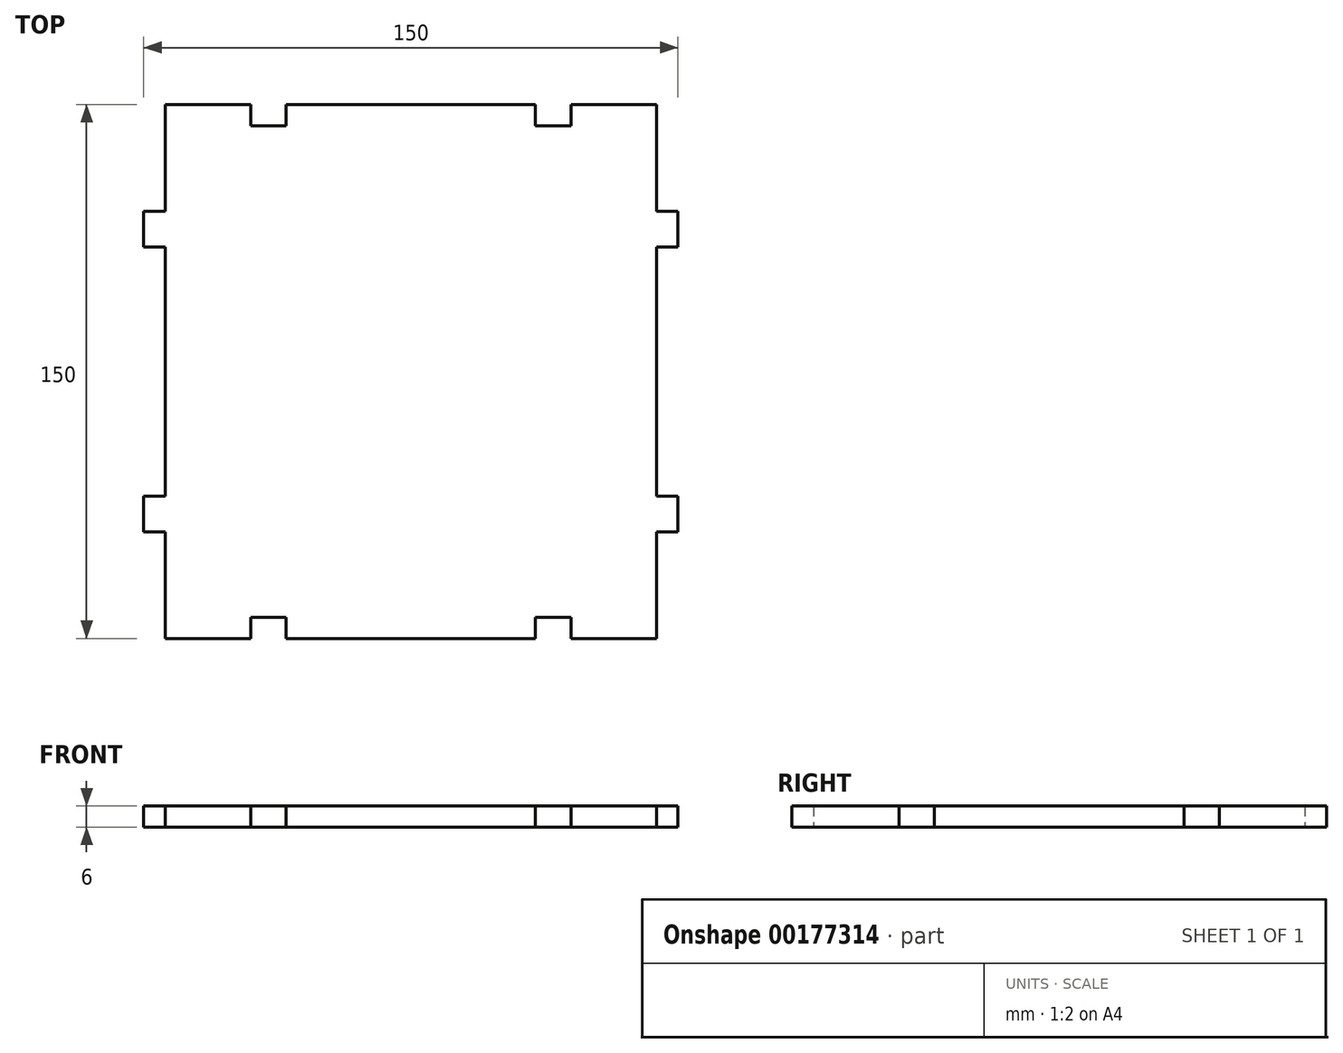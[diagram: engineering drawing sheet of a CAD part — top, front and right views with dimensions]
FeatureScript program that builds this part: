
annotation { "Feature Type Name" : "Feature", "Feature Type Description" : "" }
export const myFeature = defineFeature(function(context is Context, id is Id, definition is map)
    precondition{}
    {
        {
            var Q0;
            Q0=qCreatedBy(makeId("Top.planeOp"),FACE);
            var sketch = newSketch(context, id + "F0", { "sketchPlane" : qUnion([Q0])});
            skPoint(sketch, "E0.middle", {"position": v(4.2, -4.87) * mm});
            skLineSegment(sketch, "E1.bottom", {"start": v(73.2, -79.87) * mm, "end": v(-64.8, -79.87) * mm});
            skLineSegment(sketch, "E1.top", {"start": v(73.2, 70.13) * mm, "end": v(-64.8, 70.13) * mm});
            skLineSegment(sketch, "E1.left", {"start": v(73.2, -79.87) * mm, "end": v(73.2, 70.13) * mm});
            skLineSegment(sketch, "E1.right", {"start": v(-64.8, -79.87) * mm, "end": v(-64.8, 70.13) * mm});
            skLineSegment(sketch, "E2", {"start": v(-64.8, 70.13) * mm, "end": v(-40.8, 70.13) * mm, "construction": true});
            skLineSegment(sketch, "E3", {"start": v(-40.8, 70.13) * mm, "end": v(-40.8, 64.13) * mm});
            skLineSegment(sketch, "E4", {"start": v(-40.8, 64.13) * mm, "end": v(-30.8, 64.13) * mm});
            skLineSegment(sketch, "E5", {"start": v(-30.8, 64.13) * mm, "end": v(-30.8, 70.13) * mm});
            skLineSegment(sketch, "E6", {"start": v(4.2, -4.87) * mm, "end": v(-64.8, -4.87) * mm, "construction": true});
            skLineSegment(sketch, "E7", {"start": v(4.2, -4.87) * mm, "end": v(4.2, 70.13) * mm, "construction": true});
            skLineSegment(sketch, "E8.MirrorCS", {"start": v(49.2, 64.13) * mm, "end": v(39.2, 64.13) * mm});
            skLineSegment(sketch, "E9.MirrorCS", {"start": v(39.2, 64.13) * mm, "end": v(39.2, 70.13) * mm});
            skLineSegment(sketch, "E10.MirrorCS", {"start": v(49.2, 70.13) * mm, "end": v(49.2, 64.13) * mm});
            skLineSegment(sketch, "E11.MirrorCS", {"start": v(4.2, -4.87) * mm, "end": v(73.2, -4.87) * mm, "construction": true});
            skLineSegment(sketch, "E12.MirrorCS", {"start": v(-40.8, 58.13) * mm, "end": v(-40.8, 64.13) * mm});
            skLineSegment(sketch, "E13.MirrorCS", {"start": v(-40.8, -79.87) * mm, "end": v(-40.8, -73.87) * mm});
            skLineSegment(sketch, "E14.MirrorCS", {"start": v(-40.8, -73.87) * mm, "end": v(-30.8, -73.87) * mm});
            skLineSegment(sketch, "E15.MirrorCS", {"start": v(-30.8, -73.87) * mm, "end": v(-30.8, -79.87) * mm});
            skLineSegment(sketch, "E16.MirrorCS", {"start": v(39.2, -73.87) * mm, "end": v(39.2, -79.87) * mm});
            skLineSegment(sketch, "E17.MirrorCS", {"start": v(49.2, -73.87) * mm, "end": v(39.2, -73.87) * mm});
            skLineSegment(sketch, "E18.MirrorCS", {"start": v(49.2, -79.87) * mm, "end": v(49.2, -73.87) * mm});
            skLineSegment(sketch, "E19", {"start": v(-64.8, 70.13) * mm, "end": v(-64.8, 40.13) * mm});
            skLineSegment(sketch, "E20", {"start": v(-64.8, 40.13) * mm, "end": v(-70.8, 40.13) * mm});
            skLineSegment(sketch, "E21", {"start": v(-70.8, 40.13) * mm, "end": v(-70.8, 30.13) * mm});
            skLineSegment(sketch, "E22", {"start": v(-70.8, 30.13) * mm, "end": v(-64.8, 30.13) * mm});
            skLineSegment(sketch, "E23.MirrorCS", {"start": v(-70.8, -39.87) * mm, "end": v(-64.8, -39.87) * mm});
            skLineSegment(sketch, "E24.MirrorCS", {"start": v(-70.8, -49.87) * mm, "end": v(-70.8, -39.87) * mm});
            skLineSegment(sketch, "E25.MirrorCS", {"start": v(-64.8, -49.87) * mm, "end": v(-70.8, -49.87) * mm});
            skLineSegment(sketch, "E26.MirrorCS", {"start": v(73.2, 40.13) * mm, "end": v(79.2, 40.13) * mm});
            skLineSegment(sketch, "E27.MirrorCS", {"start": v(79.2, 40.13) * mm, "end": v(79.2, 30.13) * mm});
            skLineSegment(sketch, "E28.MirrorCS", {"start": v(79.2, 30.13) * mm, "end": v(73.2, 30.13) * mm});
            skLineSegment(sketch, "E29.MirrorCS", {"start": v(79.2, -39.87) * mm, "end": v(73.2, -39.87) * mm});
            skLineSegment(sketch, "E30.MirrorCS", {"start": v(79.2, -49.87) * mm, "end": v(79.2, -39.87) * mm});
            skLineSegment(sketch, "E31.MirrorCS", {"start": v(73.2, -49.87) * mm, "end": v(79.2, -49.87) * mm});
            skLineSegment(sketch, "E32", {"start": v(-64.8, -79.87) * mm, "end": v(-70.8, -79.87) * mm});
            skLineSegment(sketch, "E33", {"start": v(-70.8, -79.87) * mm, "end": v(-70.8, -73.87) * mm});
            skLineSegment(sketch, "E34", {"start": v(-70.8, -73.87) * mm, "end": v(-64.8, -73.87) * mm});
            skLineSegment(sketch, "E35.MirrorCS", {"start": v(-70.8, 70.13) * mm, "end": v(-70.8, 64.13) * mm});
            skLineSegment(sketch, "E36.MirrorCS", {"start": v(-64.8, 70.13) * mm, "end": v(-70.8, 70.13) * mm});
            skLineSegment(sketch, "E37.MirrorCS", {"start": v(-70.8, 64.13) * mm, "end": v(-64.8, 64.13) * mm});
            skLineSegment(sketch, "E38.MirrorCS", {"start": v(73.2, -79.87) * mm, "end": v(79.2, -79.87) * mm});
            skLineSegment(sketch, "E39.MirrorCS", {"start": v(79.2, -79.87) * mm, "end": v(79.2, -73.87) * mm});
            skLineSegment(sketch, "E40.MirrorCS", {"start": v(79.2, -73.87) * mm, "end": v(73.2, -73.87) * mm});
            skLineSegment(sketch, "E41.MirrorCS", {"start": v(73.2, 70.13) * mm, "end": v(79.2, 70.13) * mm});
            skLineSegment(sketch, "E42.MirrorCS", {"start": v(79.2, 70.13) * mm, "end": v(79.2, 64.13) * mm});
            skLineSegment(sketch, "E43.MirrorCS", {"start": v(79.2, 64.13) * mm, "end": v(73.2, 64.13) * mm});
            skSolve(sketch);
        }
        {
            var Q0;
            {var subQ6=sQuery(id+"F0.wireOp",EDGE,"E3");Q0=makeQuery(id+"F0.imprint","IMPRINT",FACE,{"disambiguationData":[TD([[makeQuery(id+"F0.imprint","IMPRINT",EDGE,{"derivedFrom":subQ6}),-1.0]])]});}
            var Q1;
            {var subQ0=sQuery(id+"F0.wireOp",EDGE,"E20");Q1=makeQuery(id+"F0.imprint","IMPRINT",FACE,{"disambiguationData":[TD([[makeQuery(id+"F0.imprint","IMPRINT",EDGE,{"derivedFrom":subQ0}),1.0]])]});}
            var Q2;
            {var subQ0=sQuery(id+"F0.wireOp",EDGE,"E23.MirrorCS");Q2=makeQuery(id+"F0.imprint","IMPRINT",FACE,{"disambiguationData":[TD([[makeQuery(id+"F0.imprint","IMPRINT",EDGE,{"derivedFrom":subQ0}),-1.0]])]});}
            var Q3;
            {var subQ0=sQuery(id+"F0.wireOp",EDGE,"E29.MirrorCS");Q3=makeQuery(id+"F0.imprint","IMPRINT",FACE,{"disambiguationData":[TD([[makeQuery(id+"F0.imprint","IMPRINT",EDGE,{"derivedFrom":subQ0}),1.0]])]});}
            var Q4;
            {var subQ0=sQuery(id+"F0.wireOp",EDGE,"E26.MirrorCS");Q4=makeQuery(id+"F0.imprint","IMPRINT",FACE,{"disambiguationData":[TD([[makeQuery(id+"F0.imprint","IMPRINT",EDGE,{"derivedFrom":subQ0}),-1.0]])]});}
            extrude(context, id + "F1", {"entities" : qUnion([Q0, Q1, Q2, Q3, Q4]), "depth" : 6 * mm});
        }
    });
